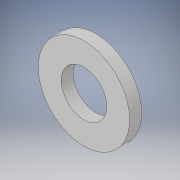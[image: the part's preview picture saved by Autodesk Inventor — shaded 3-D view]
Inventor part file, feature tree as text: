
AUTODESK INVENTOR PART (.ipt)
format: ipt  version: 2017 (Build 210142000, 142)  size: 96,768 bytes
history: native  units: in
note: dims shown in document units (in); Inventor stores cm internally (conversion verified against a paired STEP export)
features: extrude x1, sketch x1
ambient origin geometry x8: Origin, YZ Plane, XZ Plane, XY Plane, X Axis, Y Axis, Z Axis, Center Point
bodies: Solid1 (feature_tree)
feature tree (2):
  extrude  "Extrusion1"  Depth=0.05in
  sketch  "Sketch1"  dims[d0=0.19in d1=0.38in d2=0.05in d3=0.0in]
